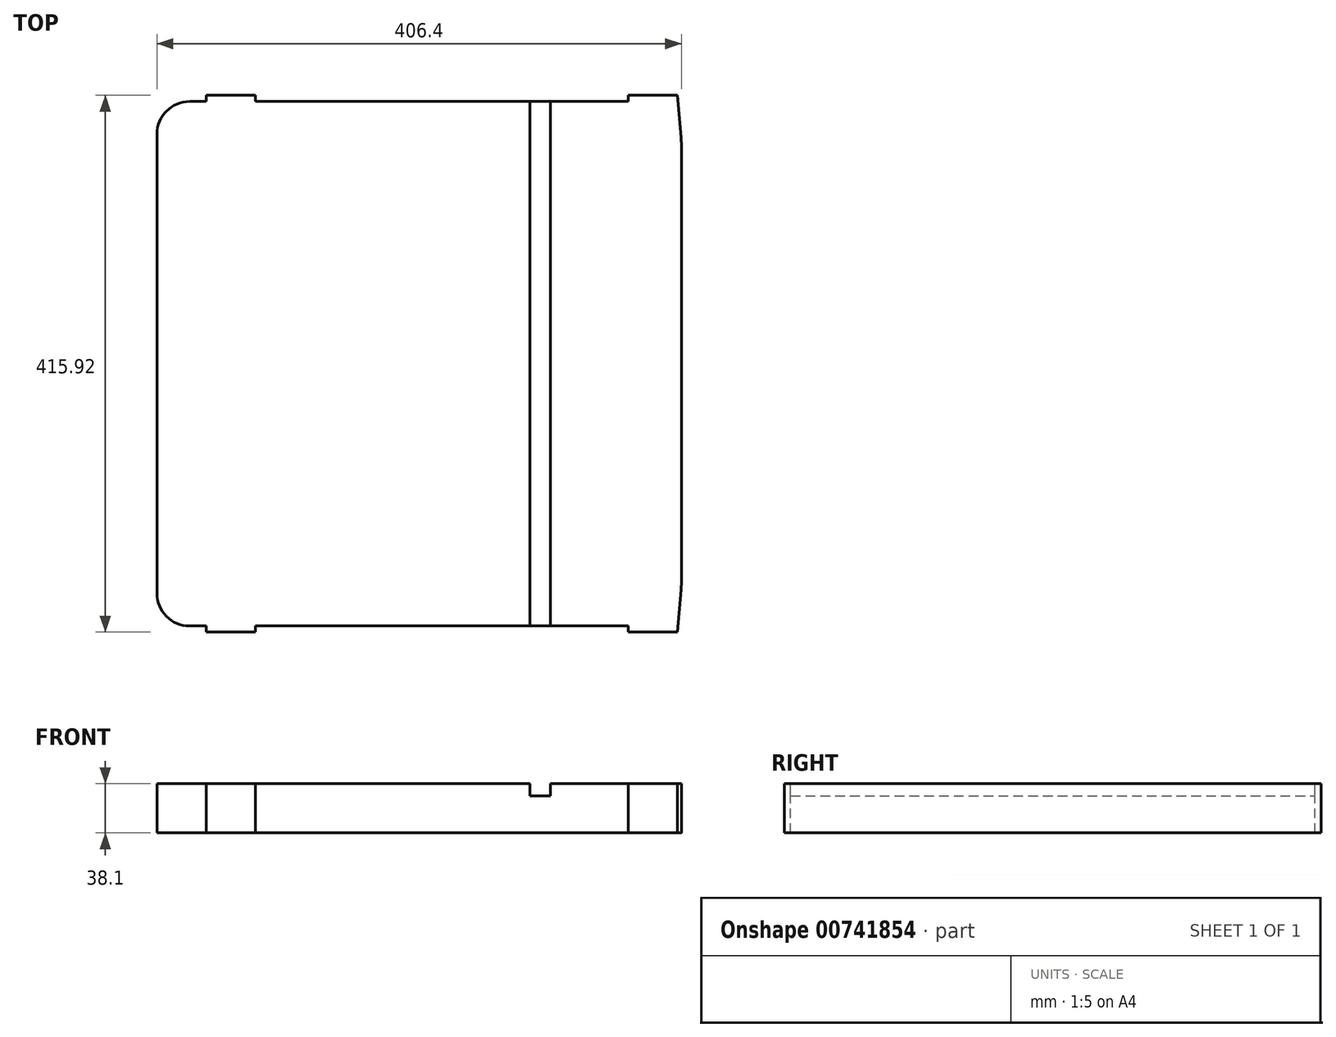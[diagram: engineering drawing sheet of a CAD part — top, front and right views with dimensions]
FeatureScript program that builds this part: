
annotation { "Feature Type Name" : "Feature", "Feature Type Description" : "" }
export const myFeature = defineFeature(function(context is Context, id is Id, definition is map)
    precondition{}
    {
        {
            var Q0;
            Q0=qCreatedBy(makeId("Top.planeOp"),FACE);
            var sketch = newSketch(context, id + "F0", { "sketchPlane" : qUnion([Q0])});
            skLineSegment(sketch, "E0.bottom", {"start": v(-177.8, 203.2) * mm, "end": v(-165.1, 203.2) * mm});
            skLineSegment(sketch, "E0.top", {"start": v(-177.8, -203.2) * mm, "end": v(-165.1, -203.2) * mm});
            skLineSegment(sketch, "E0.left", {"start": v(-203.2, 177.8) * mm, "end": v(-203.2, -177.8) * mm});
            skLineSegment(sketch, "E0.right", {"start": v(203.2, 171.76) * mm, "end": v(203.2, -171.76) * mm});
            skPoint(sketch, "E0.middle", {"position": v(0, 0) * mm});
            skLineSegment(sketch, "E1", {"start": v(-165.1, -203.2) * mm, "end": v(-165.1, -207.96) * mm});
            skLineSegment(sketch, "E2", {"start": v(-165.1, -207.96) * mm, "end": v(-127, -207.96) * mm});
            skLineSegment(sketch, "E3", {"start": v(-127, -207.96) * mm, "end": v(-127, -203.2) * mm});
            skLineSegment(sketch, "E4", {"start": v(161.92, -203.2) * mm, "end": v(161.92, -207.96) * mm});
            skLineSegment(sketch, "E5", {"start": v(161.92, -207.96) * mm, "end": v(200.02, -207.96) * mm});
            skLineSegment(sketch, "E6", {"start": v(-203.2, 0) * mm, "end": v(203.2, 0) * mm, "construction": true});
            skLineSegment(sketch, "E7.MirrorCS", {"start": v(-127, 207.96) * mm, "end": v(-127, 203.2) * mm});
            skLineSegment(sketch, "E8.MirrorCS", {"start": v(-165.1, 203.2) * mm, "end": v(-165.1, 207.96) * mm});
            skLineSegment(sketch, "E9.MirrorCS", {"start": v(-165.1, 207.96) * mm, "end": v(-127, 207.96) * mm});
            skLineSegment(sketch, "E10.MirrorCS", {"start": v(161.92, 203.2) * mm, "end": v(161.92, 207.96) * mm});
            skLineSegment(sketch, "E11.MirrorCS", {"start": v(161.92, 207.96) * mm, "end": v(200.02, 207.96) * mm});
            skLineSegment(sketch, "E12", {"start": v(200.02, -207.96) * mm, "end": v(203.04, -175.26) * mm});
            skLineSegment(sketch, "E13.MirrorCS", {"start": v(200.02, 207.96) * mm, "end": v(203.04, 175.26) * mm});
            skPoint(sketch, "E14.orphan", {"position": v(203.2, 203.2) * mm});
            skPoint(sketch, "E15.orphan", {"position": v(203.2, -203.2) * mm});
            skLineSegment(sketch, "E16.trimOffspring", {"start": v(-127, 203.2) * mm, "end": v(161.92, 203.2) * mm});
            skLineSegment(sketch, "E17.trimOffspring", {"start": v(-127, -203.2) * mm, "end": v(161.92, -203.2) * mm});
            skPoint(sketch, "E18.visualSharp", {"position": v(-203.2, 203.2) * mm});
            skArc(sketch, "E18.filletArc", {"start": v(-177.8, 203.2) * mm, "mid": v(-195.76, 195.76) * mm, "end": v(-203.2, 177.8) * mm});
            skPoint(sketch, "E19.visualSharp", {"position": v(-203.2, -203.2) * mm});
            skArc(sketch, "E19.filletArc", {"start": v(-203.2, -177.8) * mm, "mid": v(-195.76, -195.76) * mm, "end": v(-177.8, -203.2) * mm});
            skPoint(sketch, "E20.visualSharp", {"position": v(203.2, -173.52) * mm});
            skArc(sketch, "E20.filletArc", {"start": v(203.04, -175.26) * mm, "mid": v(203.16, -173.51) * mm, "end": v(203.2, -171.76) * mm});
            skPoint(sketch, "E21.visualSharp", {"position": v(203.2, 173.52) * mm});
            skArc(sketch, "E21.filletArc", {"start": v(203.2, 171.76) * mm, "mid": v(203.16, 173.51) * mm, "end": v(203.04, 175.26) * mm});
            skSolve(sketch);
        }
        {
            var Q0;
            Q0=makeQuery(id+"F0.imprint","IMPRINT",FACE,{"disambiguationData":[TD([[makeQuery(id+"F0.imprint","IMPRINT",EDGE,{"derivedFrom":sQuery(id+"F0.wireOp",EDGE,"E0.bottom")}),-1.0]])]});
            extrude(context, id + "F1", {"entities" : qUnion([Q0]), "oppositeDirection" : true, "depth" : 38.1 * mm, "offsetDistance" : 25.4 * mm});
        }
        {
            var Q0;
            Q0=makeQuery(id+"F1.opExtrude","CAP_FACE",FACE,{"disambiguationData":[OSD([sQuery(id+"F0.wireOp",EDGE,"E0.bottom"),sQuery(id+"F0.wireOp",EDGE,"E0.top"),sQuery(id+"F0.wireOp",EDGE,"E0.left"),sQuery(id+"F0.wireOp",EDGE,"E0.right"),sQuery(id+"F0.wireOp",EDGE,"E1"),sQuery(id+"F0.wireOp",EDGE,"E2"),sQuery(id+"F0.wireOp",EDGE,"E3"),sQuery(id+"F0.wireOp",EDGE,"E4"),sQuery(id+"F0.wireOp",EDGE,"E5"),sQuery(id+"F0.wireOp",EDGE,"E7.MirrorCS"),sQuery(id+"F0.wireOp",EDGE,"E8.MirrorCS"),sQuery(id+"F0.wireOp",EDGE,"E9.MirrorCS"),sQuery(id+"F0.wireOp",EDGE,"E10.MirrorCS"),sQuery(id+"F0.wireOp",EDGE,"E11.MirrorCS"),sQuery(id+"F0.wireOp",EDGE,"E12"),sQuery(id+"F0.wireOp",EDGE,"E13.MirrorCS"),sQuery(id+"F0.wireOp",EDGE,"E16.trimOffspring"),sQuery(id+"F0.wireOp",EDGE,"E17.trimOffspring"),sQuery(id+"F0.wireOp",EDGE,"E18.filletArc"),sQuery(id+"F0.wireOp",EDGE,"E19.filletArc"),sQuery(id+"F0.wireOp",EDGE,"E20.filletArc"),sQuery(id+"F0.wireOp",EDGE,"E21.filletArc")])],"isStart":true});
            var sketch = newSketch(context, id + "F2", { "sketchPlane" : qUnion([Q0])});
            skLineSegment(sketch, "E22.bottom", {"start": v(85.73, -203.2) * mm, "end": v(101.6, -203.2) * mm});
            skLineSegment(sketch, "E22.top", {"start": v(85.72, 203.2) * mm, "end": v(101.6, 203.2) * mm});
            skLineSegment(sketch, "E22.left", {"start": v(85.73, -203.2) * mm, "end": v(85.72, 203.2) * mm});
            skLineSegment(sketch, "E22.right", {"start": v(101.6, -203.2) * mm, "end": v(101.6, 203.2) * mm});
            skSolve(sketch);
        }
        {
            var Q0;
            Q0=makeQuery(id+"F2.imprint","IMPRINT",FACE,{"disambiguationData":[TD([[makeQuery(id+"F2.imprint","IMPRINT",EDGE,{"derivedFrom":sQuery(id+"F2.wireOp",EDGE,"E22.bottom")}),1.0]])]});
            extrude(context, id + "F3", {"entities" : qUnion([Q0]), "operationType" : NewBodyOperationType.REMOVE, "oppositeDirection" : true, "depth" : 9.52 * mm, "offsetDistance" : 25.4 * mm});
        }
    });
